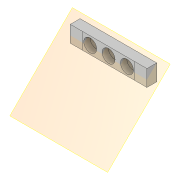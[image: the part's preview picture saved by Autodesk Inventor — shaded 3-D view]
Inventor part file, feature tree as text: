
AUTODESK INVENTOR PART (.ipt)
format: ipt  version: 2019 (Build 230136000, 136)  size: 130,560 bytes
history: native  units: in
note: dims shown in document units (in); Inventor stores cm internally (conversion verified against a paired STEP export)
features: sketch x4, extrude x3, plane x1, hole x1
ambient origin geometry x8: Origin, YZ Plane, XZ Plane, XY Plane, X Axis, Y Axis, Z Axis, Center Point
bodies: Solid1 (feature_tree)
feature tree (9):
  extrude  "Extrusion1"  Depth=1.4764in
  extrude  "Extrusion2"  Depth=1.0in
  plane  "Work Plane1"
  extrude  "Extrusion3"  Depth=0.3937in TaperAngle=0.0deg
  hole  "Hole1"  [1 undecoded]
  sketch  "Sketch1"  dims[d0=0.315in d1=1.4764in]
  sketch  "Sketch2"  dims[d3=0.189in d4=0.0in d5=1.0in]
  sketch  "Sketch3"  dims[d6=0.0in d7=0.0in d9=0.3937in d10=0.0in]
  sketch  "Sketch6"  dims[d17=0.3543in d18=0.7087in d19=0.3543in d20=0.3543in d21=0.3543in d22=0.3543in d23=0.248in d24=0.2362in d25=0.1575in d26=0.0787in d27=90.0deg d28=0.122in d29=0.0in d30=0.3543in]
note: 1 required parameter value undecoded (feature->parameter linkage not recoverable at this tier; creation-order binding heuristic only, values carry confidence <= 0.55)
